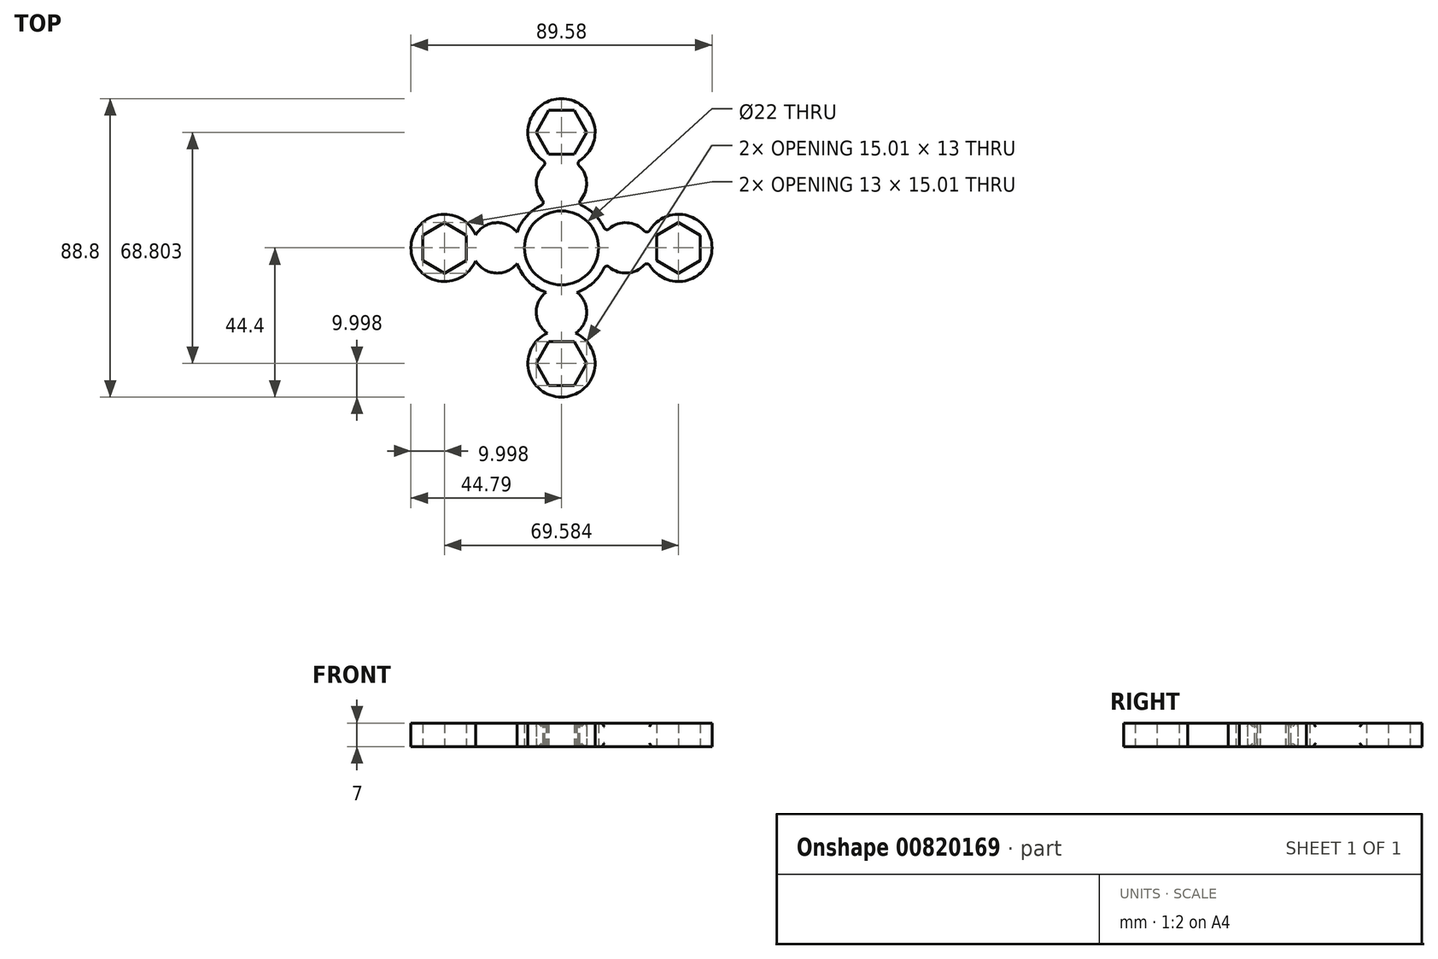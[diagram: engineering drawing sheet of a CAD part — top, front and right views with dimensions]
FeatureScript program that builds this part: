
annotation { "Feature Type Name" : "Feature", "Feature Type Description" : "" }
export const myFeature = defineFeature(function(context is Context, id is Id, definition is map)
    precondition{}
    {
        {
            var Q0;
            Q0=qCreatedBy(makeId("Top.planeOp"),FACE);
            var sketch = newSketch(context, id + "F0", { "sketchPlane" : qUnion([Q0])});
            skCircle(sketch, "E0", {"center": v(0, 0) * mm, "radius": 11 * mm});
            skCircle(sketch, "E1", {"center": v(0, 0) * mm, "radius": 14 * mm});
            skCircle(sketch, "E2", {"center": v(19.1, 0) * mm, "radius": 7.5 * mm});
            skCircle(sketch, "E3.MirrorC", {"center": v(-19.1, 0) * mm, "radius": 7.5 * mm});
            skCircle(sketch, "E4", {"center": v(0, 19.11) * mm, "radius": 7.5 * mm});
            skCircle(sketch, "E5.MirrorC", {"center": v(0, -19.11) * mm, "radius": 7.5 * mm});
            skCircle(sketch, "E6", {"center": v(34.8, 0) * mm, "radius": 10 * mm});
            skCircle(sketch, "E7.MirrorC", {"center": v(-34.8, 0) * mm, "radius": 10 * mm});
            skCircle(sketch, "E8", {"center": v(0, 34.4) * mm, "radius": 10 * mm});
            skCircle(sketch, "E9.MirrorC", {"center": v(0, -34.4) * mm, "radius": 10 * mm});
            skCircle(sketch, "E10.cCircle", {"center": v(34.8, 0) * mm, "radius": 6.5 * mm, "construction": true});
            skLineSegment(sketch, "E10.0", {"start": v(41.3, 3.75) * mm, "end": v(41.3, -3.75) * mm});
            skLineSegment(sketch, "E10.1", {"start": v(41.3, -3.75) * mm, "end": v(34.8, -7.5) * mm});
            skLineSegment(sketch, "E10.2", {"start": v(34.8, -7.5) * mm, "end": v(28.3, -3.75) * mm});
            skLineSegment(sketch, "E10.3", {"start": v(28.3, -3.75) * mm, "end": v(28.3, 3.75) * mm});
            skLineSegment(sketch, "E10.4", {"start": v(28.3, 3.75) * mm, "end": v(34.8, 7.5) * mm});
            skLineSegment(sketch, "E10.5", {"start": v(34.8, 7.5) * mm, "end": v(41.3, 3.75) * mm});
            skPoint(sketch, "E10.0.midPoint", {"position": v(41.3, 0) * mm});
            skLineSegment(sketch, "E11.MirrorCS", {"start": v(-28.3, -3.75) * mm, "end": v(-28.3, 3.75) * mm});
            skLineSegment(sketch, "E12.MirrorCS", {"start": v(-28.3, 3.75) * mm, "end": v(-34.8, 7.5) * mm});
            skCircle(sketch, "E13.MirrorC", {"center": v(-34.8, 0) * mm, "radius": 6.5 * mm, "construction": true});
            skLineSegment(sketch, "E14.MirrorCS", {"start": v(-34.8, 7.5) * mm, "end": v(-41.3, 3.75) * mm});
            skLineSegment(sketch, "E15.MirrorCS", {"start": v(-41.3, 3.75) * mm, "end": v(-41.3, -3.75) * mm});
            skLineSegment(sketch, "E16.MirrorCS", {"start": v(-41.3, -3.75) * mm, "end": v(-34.8, -7.5) * mm});
            skLineSegment(sketch, "E17.MirrorCS", {"start": v(-34.8, -7.5) * mm, "end": v(-28.3, -3.75) * mm});
            skCircle(sketch, "E18.cCircle", {"center": v(0, 34.4) * mm, "radius": 6.5 * mm, "construction": true});
            skLineSegment(sketch, "E18.0", {"start": v(-3.75, 40.9) * mm, "end": v(3.75, 40.9) * mm});
            skLineSegment(sketch, "E18.1", {"start": v(3.75, 40.9) * mm, "end": v(7.5, 34.4) * mm});
            skLineSegment(sketch, "E18.2", {"start": v(7.5, 34.4) * mm, "end": v(3.75, 27.9) * mm});
            skLineSegment(sketch, "E18.3", {"start": v(3.75, 27.9) * mm, "end": v(-3.75, 27.9) * mm});
            skLineSegment(sketch, "E18.4", {"start": v(-3.75, 27.9) * mm, "end": v(-7.5, 34.4) * mm});
            skLineSegment(sketch, "E18.5", {"start": v(-7.5, 34.4) * mm, "end": v(-3.75, 40.9) * mm});
            skPoint(sketch, "E18.0.midPoint", {"position": v(0, 40.9) * mm});
            skCircle(sketch, "E19.MirrorC", {"center": v(0, -34.4) * mm, "radius": 6.5 * mm, "construction": true});
            skLineSegment(sketch, "E20.MirrorCS", {"start": v(3.75, -27.9) * mm, "end": v(-3.75, -27.9) * mm});
            skLineSegment(sketch, "E21.MirrorCS", {"start": v(7.5, -34.4) * mm, "end": v(3.75, -27.9) * mm});
            skLineSegment(sketch, "E22.MirrorCS", {"start": v(-3.75, -27.9) * mm, "end": v(-7.5, -34.4) * mm});
            skLineSegment(sketch, "E23.MirrorCS", {"start": v(3.75, -40.9) * mm, "end": v(7.5, -34.4) * mm});
            skLineSegment(sketch, "E24.MirrorCS", {"start": v(-3.75, -40.9) * mm, "end": v(3.75, -40.9) * mm});
            skLineSegment(sketch, "E25.MirrorCS", {"start": v(-7.5, -34.4) * mm, "end": v(-3.75, -40.9) * mm});
            skSolve(sketch);
        }
        {
            var Q0;
            Q0 = qSketchRegion(id + "F0", true);
            extrude(context, id + "F1", {"entities" : qUnion([Q0]), "depth" : 7 * mm, "offsetDistance" : 25 * mm});
        }
        {
            var Q0;
            {var subQ0=sQuery(id+"F0.wireOp",EDGE,"E3.MirrorC");Q0=makeQuery(id+"F1.opExtrude","SWEPT_FACE",FACE,{"disambiguationData":[OSD([subQ0]),TDD([makeQuery(id+"F0.imprint","IMPRINT",EDGE,{"disambiguationData":[TD([[makeQuery(id+"F0.imprint","INTERSECT",VERTEX,{"disambiguationData":[OD(1.0)],"derivedFrom":[sQuery(id+"F0.wireOp",EDGE,"E1"),subQ0]}),-1.0]])],"derivedFrom":subQ0})])]});}
            var Q1;
            {var subQ0=sQuery(id+"F0.wireOp",EDGE,"E5.MirrorC");Q1=makeQuery(id+"F1.opExtrude","SWEPT_FACE",FACE,{"disambiguationData":[OSD([subQ0]),TDD([makeQuery(id+"F0.imprint","IMPRINT",EDGE,{"disambiguationData":[TD([[makeQuery(id+"F0.imprint","INTERSECT",VERTEX,{"disambiguationData":[OD(1.0)],"derivedFrom":[sQuery(id+"F0.wireOp",EDGE,"E1"),subQ0]}),-1.0]])],"derivedFrom":subQ0})])]});}
            var Q2;
            {var subQ0=sQuery(id+"F0.wireOp",EDGE,"E3.MirrorC");Q2=makeQuery(id+"F1.opExtrude","SWEPT_FACE",FACE,{"disambiguationData":[OSD([subQ0]),TDD([makeQuery(id+"F0.imprint","IMPRINT",EDGE,{"disambiguationData":[TD([[makeQuery(id+"F0.imprint","INTERSECT",VERTEX,{"disambiguationData":[OD(0.0)],"derivedFrom":[sQuery(id+"F0.wireOp",EDGE,"E1"),subQ0]}),1.0]])],"derivedFrom":subQ0})])]});}
            var Q3;
            {var subQ0=sQuery(id+"F0.wireOp",EDGE,"E4");Q3=makeQuery(id+"F1.opExtrude","SWEPT_FACE",FACE,{"disambiguationData":[OSD([subQ0]),TDD([makeQuery(id+"F0.imprint","IMPRINT",EDGE,{"disambiguationData":[TD([[makeQuery(id+"F0.imprint","INTERSECT",VERTEX,{"disambiguationData":[OD(1.0)],"derivedFrom":[sQuery(id+"F0.wireOp",EDGE,"E1"),subQ0]}),1.0]])],"derivedFrom":subQ0})])]});}
            var Q4;
            {var subQ0=sQuery(id+"F0.wireOp",EDGE,"E4");Q4=makeQuery(id+"F1.opExtrude","SWEPT_FACE",FACE,{"disambiguationData":[OSD([subQ0]),TDD([makeQuery(id+"F0.imprint","IMPRINT",EDGE,{"disambiguationData":[TD([[makeQuery(id+"F0.imprint","INTERSECT",VERTEX,{"disambiguationData":[OD(0.0)],"derivedFrom":[sQuery(id+"F0.wireOp",EDGE,"E1"),subQ0]}),-1.0]])],"derivedFrom":subQ0})])]});}
            var Q5;
            {var subQ0=sQuery(id+"F0.wireOp",EDGE,"E2");Q5=makeQuery(id+"F1.opExtrude","SWEPT_FACE",FACE,{"disambiguationData":[OSD([subQ0]),TDD([makeQuery(id+"F0.imprint","IMPRINT",EDGE,{"disambiguationData":[TD([[makeQuery(id+"F0.imprint","INTERSECT",VERTEX,{"disambiguationData":[OD(0.0)],"derivedFrom":[sQuery(id+"F0.wireOp",EDGE,"E1"),subQ0]}),1.0]])],"derivedFrom":subQ0})])]});}
            var Q6;
            {var subQ0=sQuery(id+"F0.wireOp",EDGE,"E2");Q6=makeQuery(id+"F1.opExtrude","SWEPT_FACE",FACE,{"disambiguationData":[OSD([subQ0]),TDD([makeQuery(id+"F0.imprint","IMPRINT",EDGE,{"disambiguationData":[TD([[makeQuery(id+"F0.imprint","INTERSECT",VERTEX,{"disambiguationData":[OD(1.0)],"derivedFrom":[sQuery(id+"F0.wireOp",EDGE,"E1"),subQ0]}),-1.0]])],"derivedFrom":subQ0})])]});}
            var Q7;
            {var subQ0=sQuery(id+"F0.wireOp",EDGE,"E5.MirrorC");Q7=makeQuery(id+"F1.opExtrude","SWEPT_FACE",FACE,{"disambiguationData":[OSD([subQ0]),TDD([makeQuery(id+"F0.imprint","IMPRINT",EDGE,{"disambiguationData":[TD([[makeQuery(id+"F0.imprint","INTERSECT",VERTEX,{"disambiguationData":[OD(0.0)],"derivedFrom":[sQuery(id+"F0.wireOp",EDGE,"E1"),subQ0]}),1.0]])],"derivedFrom":subQ0})])]});}
            fillet(context, id + "F2", {"entities" : qUnion([Q0, Q1, Q2, Q3, Q4, Q5, Q6, Q7]), "radius" : 1 * mm, "tangentPropagation" : true, "allowEdgeOverflow" : false});
        }
    });
